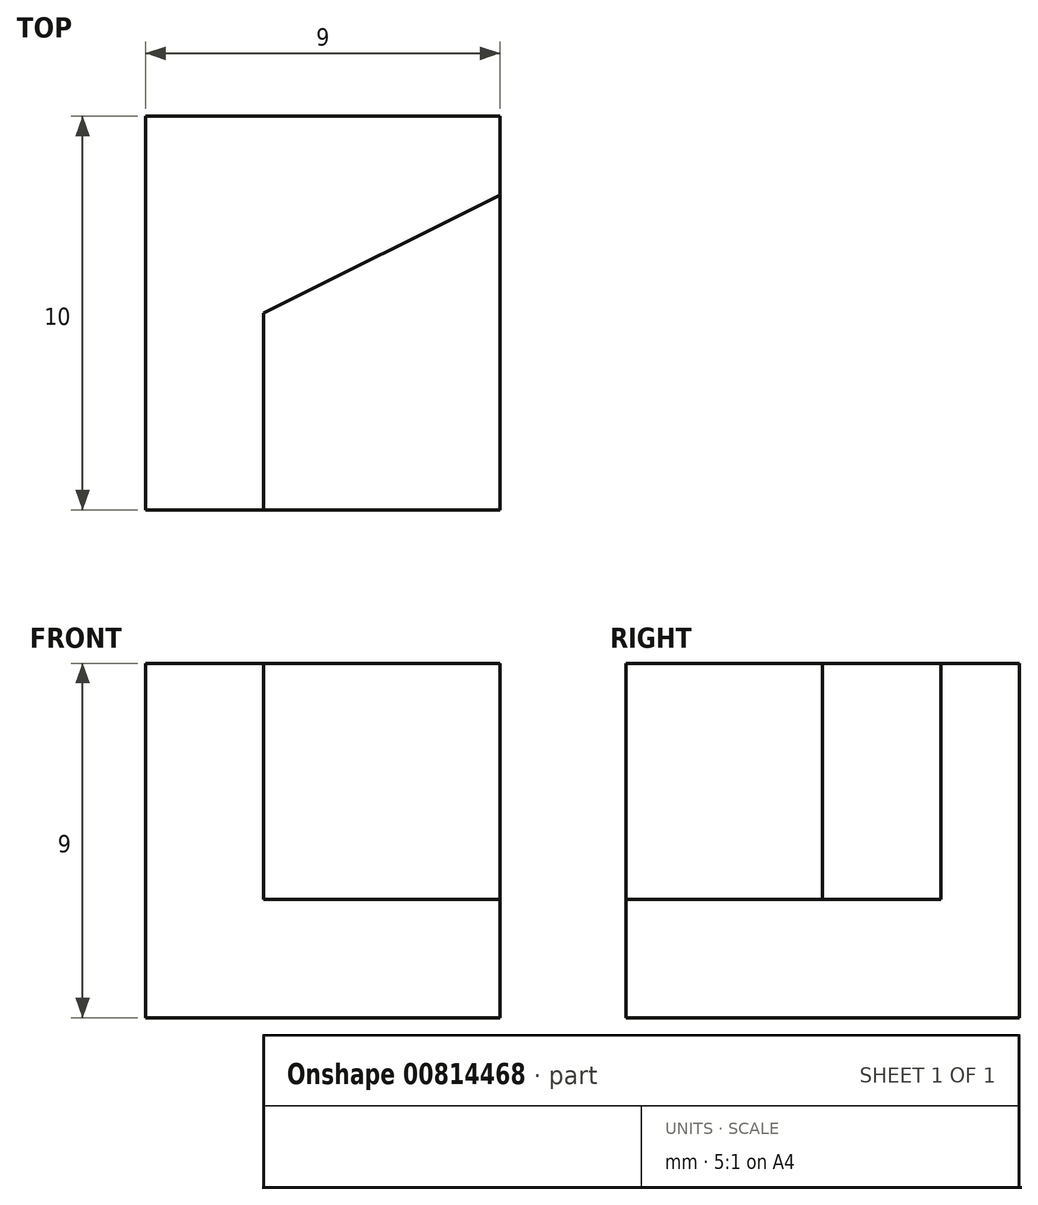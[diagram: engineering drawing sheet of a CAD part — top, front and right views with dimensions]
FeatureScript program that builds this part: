
annotation { "Feature Type Name" : "Feature", "Feature Type Description" : "" }
export const myFeature = defineFeature(function(context is Context, id is Id, definition is map)
    precondition{}
    {
        {
            var Q0;
            Q0=qCreatedBy(makeId("Top.planeOp"),FACE);
            var sketch = newSketch(context, id + "F0", { "sketchPlane" : qUnion([Q0])});
            skLineSegment(sketch, "E0.bottom", {"start": v(0, 0) * mm, "end": v(9, 0) * mm});
            skLineSegment(sketch, "E0.top", {"start": v(0, 10) * mm, "end": v(9, 10) * mm});
            skLineSegment(sketch, "E0.left", {"start": v(0, 0) * mm, "end": v(0, 10) * mm});
            skLineSegment(sketch, "E0.right", {"start": v(9, 0) * mm, "end": v(9, 10) * mm});
            skLineSegment(sketch, "E1", {"start": v(3, 0) * mm, "end": v(3, 5) * mm});
            skLineSegment(sketch, "E2", {"start": v(3, 5) * mm, "end": v(9, 8) * mm});
            skSolve(sketch);
        }
        {
            var Q0;
            Q0 = qSketchRegion(id + "F0", true);
            extrude(context, id + "F1", {"entities" : qUnion([Q0]), "depth" : 3 * mm, "offsetDistance" : 25 * mm});
        }
        {
            var Q0;
            {var subQ1=sQuery(id+"F0.wireOp",EDGE,"E0.top");Q0=makeQuery(id+"F0.imprint","IMPRINT",FACE,{"disambiguationData":[TD([[makeQuery(id+"F0.imprint","IMPRINT",EDGE,{"derivedFrom":subQ1}),-1.0]])]});}
            extrude(context, id + "F2", {"entities" : qUnion([Q0]), "operationType" : NewBodyOperationType.ADD, "depth" : 9 * mm, "offsetDistance" : 25 * mm});
        }
        {
            var Q0;
            Q0=makeQuery(id+"F1.opExtrude","CAP_FACE",FACE,{"disambiguationData":[OSD([sQuery(id+"F0.wireOp",EDGE,"E0.bottom"),sQuery(id+"F0.wireOp",EDGE,"E0.top"),sQuery(id+"F0.wireOp",EDGE,"E0.left"),sQuery(id+"F0.wireOp",EDGE,"E0.right")])],"isStart":false});
            var sketch = newSketch(context, id + "F3", { "sketchPlane" : qUnion([Q0])});
            skPoint(sketch, "E3", {"position": v(9, 3) * mm});
            skPoint(sketch, "E4", {"position": v(6, 0) * mm});
            skSolve(sketch);
        }
        {
            var Q0;
            Q0=makeQuery(id+"F1.opExtrude","CAP_EDGE",EDGE,{"disambiguationData":[OSD([sQuery(id+"F0.wireOp",EDGE,"E0.bottom")])],"isStart":false});
            cPoint(context, id + "F4", {"entities" : qUnion([Q0]), "parameter" : 0.5});
        }
        {
            var Q0;
            Q0 = qCreatedBy(id + "F4" ,VERTEX);
            var Q1;
            Q1=sQuery(id+"F3.wireOp",VERTEX,"E3");
            var Q2;
            Q2=makeQuery(id+"F1.opExtrude","CAP_VERTEX",VERTEX,{"disambiguationData":[OSD([sQuery(id+"F0.wireOp",EDGE,"E0.bottom"),sQuery(id+"F0.wireOp",EDGE,"E0.right")])],"isStart":true});
            cPlane(context, id + "F5", {"entities" : qUnion([Q0, Q1, Q2]), "cplaneType" : CPlaneType.THREE_POINT, "offset" : 25 * mm, "width" : 150 * mm, "height" : 150 * mm});
        }
        {
            var Q0;
            Q0=qCreatedBy(id+"F5.planeOp",FACE);
            var sketch = newSketch(context, id + "F6", { "sketchPlane" : qUnion([Q0])});
            skPoint(sketch, "E5.0", {"position": v(3.67, -6.36) * mm});
            skPoint(sketch, "E6.0", {"position": v(3.67, -2.12) * mm});
            skPoint(sketch, "E7.0", {"position": v(7.35, -4.24) * mm});
            skLineSegment(sketch, "E8", {"start": v(3.67, -2.12) * mm, "end": v(7.35, -4.24) * mm});
            skLineSegment(sketch, "E9", {"start": v(7.35, -4.24) * mm, "end": v(3.67, -6.36) * mm});
            skLineSegment(sketch, "E10", {"start": v(3.67, -2.12) * mm, "end": v(3.67, -6.36) * mm});
            skSolve(sketch);
        }
        {
            var Q0;
            Q0 = qSketchRegion(id + "F6", true);
            extrude(context, id + "F7", {"entities" : qUnion([Q0]), "operationType" : NewBodyOperationType.REMOVE, "endBound" : BoundingType.THROUGH_ALL, "depth" : 25 * mm, "offsetDistance" : 25 * mm});
        }
    });
